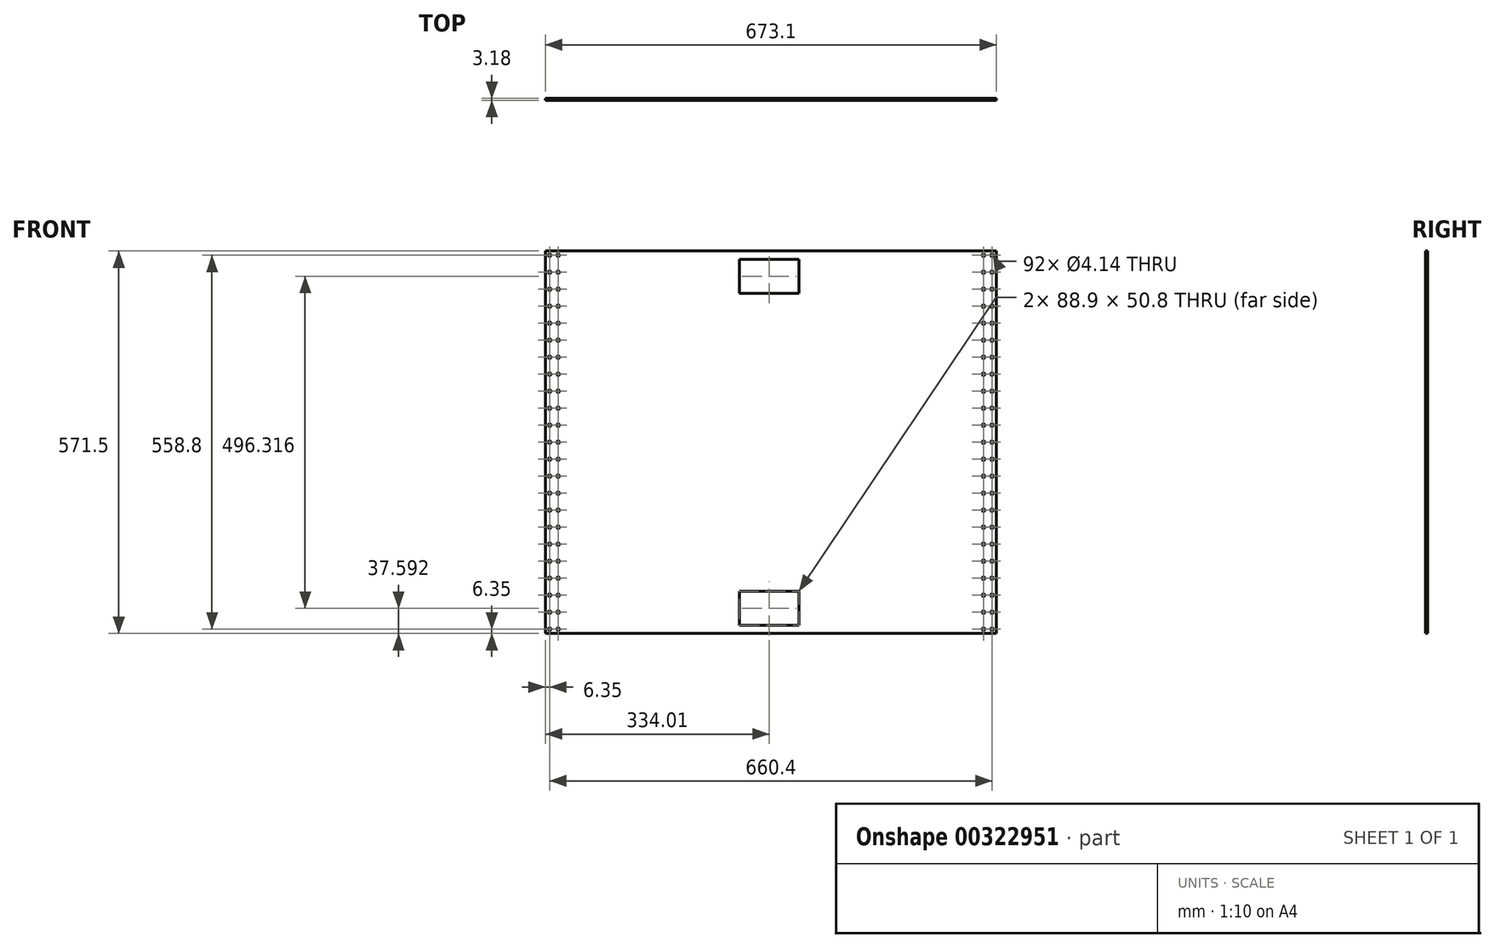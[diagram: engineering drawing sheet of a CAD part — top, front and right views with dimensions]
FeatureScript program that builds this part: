
annotation { "Feature Type Name" : "Feature", "Feature Type Description" : "" }
export const myFeature = defineFeature(function(context is Context, id is Id, definition is map)
    precondition{}
    {
        {
            var Q0;
            Q0=qCreatedBy(makeId("Front.planeOp"),FACE);
            var sketch = newSketch(context, id + "F0", { "sketchPlane" : qUnion([Q0])});
            skLineSegment(sketch, "E0.bottom", {"start": v(336.55, -285.75) * mm, "end": v(-336.55, -285.75) * mm});
            skLineSegment(sketch, "E0.top", {"start": v(336.55, 285.75) * mm, "end": v(-336.55, 285.75) * mm});
            skLineSegment(sketch, "E0.left", {"start": v(336.55, -285.75) * mm, "end": v(336.55, 285.75) * mm});
            skLineSegment(sketch, "E0.right", {"start": v(-336.55, -285.75) * mm, "end": v(-336.55, 285.75) * mm});
            skPoint(sketch, "E0.middle", {"position": v(0, 0) * mm});
            skSolve(sketch);
        }
        {
            var Q0;
            Q0 = qSketchRegion(id + "F0", true);
            extrude(context, id + "F1", {"entities" : qUnion([Q0]), "depth" : 3.17 * mm});
        }
        {
            var Q0;
            Q0=makeQuery(id+"F1.opExtrude","CAP_FACE",FACE,{"disambiguationData":[OSD([sQuery(id+"F0.wireOp",EDGE,"E0.bottom"),sQuery(id+"F0.wireOp",EDGE,"E0.top"),sQuery(id+"F0.wireOp",EDGE,"E0.left"),sQuery(id+"F0.wireOp",EDGE,"E0.right")])],"isStart":false});
            var sketch = newSketch(context, id + "F2", { "sketchPlane" : qUnion([Q0])});
            skCircle(sketch, "E1", {"center": v(330.2, -279.4) * mm, "radius": 2.07 * mm});
            skCircle(sketch, "E2.0.1.0", {"center": v(330.2, -254) * mm, "radius": 2.07 * mm});
            skCircle(sketch, "E2.0.2.0", {"center": v(330.2, -228.6) * mm, "radius": 2.07 * mm});
            skCircle(sketch, "E2.0.3.0", {"center": v(330.2, -203.2) * mm, "radius": 2.07 * mm});
            skCircle(sketch, "E2.0.4.0", {"center": v(330.2, -177.8) * mm, "radius": 2.07 * mm});
            skCircle(sketch, "E2.0.5.0", {"center": v(330.2, -152.4) * mm, "radius": 2.07 * mm});
            skCircle(sketch, "E2.1.0.0", {"center": v(317.5, -279.4) * mm, "radius": 2.07 * mm});
            skCircle(sketch, "E2.1.1.0", {"center": v(317.5, -254) * mm, "radius": 2.07 * mm});
            skCircle(sketch, "E2.1.2.0", {"center": v(317.5, -228.6) * mm, "radius": 2.07 * mm});
            skCircle(sketch, "E2.1.3.0", {"center": v(317.5, -203.2) * mm, "radius": 2.07 * mm});
            skCircle(sketch, "E2.1.4.0", {"center": v(317.5, -177.8) * mm, "radius": 2.07 * mm});
            skCircle(sketch, "E2.1.5.0", {"center": v(317.5, -152.4) * mm, "radius": 2.07 * mm});
            skLineSegment(sketch, "E2.direction1", {"start": v(330.2, -279.4) * mm, "end": v(317.5, -279.4) * mm, "construction": true});
            skLineSegment(sketch, "E2.direction2", {"start": v(330.2, -279.4) * mm, "end": v(330.2, -254) * mm, "construction": true});
            skCircle(sketch, "E3.0.0.6", {"center": v(330.2, -127) * mm, "radius": 2.07 * mm});
            skCircle(sketch, "E3.0.0.7", {"center": v(330.2, -101.6) * mm, "radius": 2.07 * mm});
            skCircle(sketch, "E3.0.0.8", {"center": v(330.2, -76.2) * mm, "radius": 2.07 * mm});
            skCircle(sketch, "E3.0.0.9", {"center": v(330.2, -50.8) * mm, "radius": 2.07 * mm});
            skCircle(sketch, "E3.0.0.10", {"center": v(330.2, -25.4) * mm, "radius": 2.07 * mm});
            skCircle(sketch, "E3.0.0.11", {"center": v(330.2, 0) * mm, "radius": 2.07 * mm});
            skCircle(sketch, "E3.0.0.12", {"center": v(330.2, 25.4) * mm, "radius": 2.07 * mm});
            skCircle(sketch, "E3.0.0.13", {"center": v(330.2, 50.8) * mm, "radius": 2.07 * mm});
            skCircle(sketch, "E3.0.0.14", {"center": v(330.2, 76.2) * mm, "radius": 2.07 * mm});
            skCircle(sketch, "E3.0.0.15", {"center": v(330.2, 101.6) * mm, "radius": 2.07 * mm});
            skCircle(sketch, "E3.0.0.16", {"center": v(330.2, 127) * mm, "radius": 2.07 * mm});
            skCircle(sketch, "E3.0.0.17", {"center": v(330.2, 152.4) * mm, "radius": 2.07 * mm});
            skCircle(sketch, "E3.0.0.18", {"center": v(330.2, 177.8) * mm, "radius": 2.07 * mm});
            skCircle(sketch, "E3.0.0.19", {"center": v(330.2, 203.2) * mm, "radius": 2.07 * mm});
            skCircle(sketch, "E3.0.1.6", {"center": v(317.5, -127) * mm, "radius": 2.07 * mm});
            skCircle(sketch, "E3.0.1.7", {"center": v(317.5, -101.6) * mm, "radius": 2.07 * mm});
            skCircle(sketch, "E3.0.1.8", {"center": v(317.5, -76.2) * mm, "radius": 2.07 * mm});
            skCircle(sketch, "E3.0.1.9", {"center": v(317.5, -50.8) * mm, "radius": 2.07 * mm});
            skCircle(sketch, "E3.0.1.10", {"center": v(317.5, -25.4) * mm, "radius": 2.07 * mm});
            skCircle(sketch, "E3.0.1.11", {"center": v(317.5, 0) * mm, "radius": 2.07 * mm});
            skCircle(sketch, "E3.0.1.12", {"center": v(317.5, 25.4) * mm, "radius": 2.07 * mm});
            skCircle(sketch, "E3.0.1.13", {"center": v(317.5, 50.8) * mm, "radius": 2.07 * mm});
            skCircle(sketch, "E3.0.1.14", {"center": v(317.5, 76.2) * mm, "radius": 2.07 * mm});
            skCircle(sketch, "E3.0.1.15", {"center": v(317.5, 101.6) * mm, "radius": 2.07 * mm});
            skCircle(sketch, "E3.0.1.16", {"center": v(317.5, 127) * mm, "radius": 2.07 * mm});
            skCircle(sketch, "E3.0.1.17", {"center": v(317.5, 152.4) * mm, "radius": 2.07 * mm});
            skCircle(sketch, "E3.0.1.18", {"center": v(317.5, 177.8) * mm, "radius": 2.07 * mm});
            skCircle(sketch, "E3.0.1.19", {"center": v(317.5, 203.2) * mm, "radius": 2.07 * mm});
            skCircle(sketch, "E4.0.0.20", {"center": v(330.2, 228.6) * mm, "radius": 2.07 * mm});
            skCircle(sketch, "E4.0.0.21", {"center": v(330.2, 254) * mm, "radius": 2.07 * mm});
            skCircle(sketch, "E4.0.0.22", {"center": v(330.2, 279.4) * mm, "radius": 2.07 * mm});
            skCircle(sketch, "E4.0.1.20", {"center": v(317.5, 228.6) * mm, "radius": 2.07 * mm});
            skCircle(sketch, "E4.0.1.21", {"center": v(317.5, 254) * mm, "radius": 2.07 * mm});
            skCircle(sketch, "E4.0.1.22", {"center": v(317.5, 279.4) * mm, "radius": 2.07 * mm});
            skCircle(sketch, "E5", {"center": v(-330.2, -279.4) * mm, "radius": 2.07 * mm});
            skCircle(sketch, "E6.0.1.0", {"center": v(-330.2, -254) * mm, "radius": 2.07 * mm});
            skCircle(sketch, "E6.0.2.0", {"center": v(-330.2, -228.6) * mm, "radius": 2.07 * mm});
            skCircle(sketch, "E6.0.3.0", {"center": v(-330.2, -203.2) * mm, "radius": 2.07 * mm});
            skCircle(sketch, "E6.0.4.0", {"center": v(-330.2, -177.8) * mm, "radius": 2.07 * mm});
            skCircle(sketch, "E6.0.5.0", {"center": v(-330.2, -152.4) * mm, "radius": 2.07 * mm});
            skCircle(sketch, "E6.0.6.0", {"center": v(-330.2, -127) * mm, "radius": 2.07 * mm});
            skCircle(sketch, "E6.0.7.0", {"center": v(-330.2, -101.6) * mm, "radius": 2.07 * mm});
            skCircle(sketch, "E6.0.8.0", {"center": v(-330.2, -76.2) * mm, "radius": 2.07 * mm});
            skCircle(sketch, "E6.0.9.0", {"center": v(-330.2, -50.8) * mm, "radius": 2.07 * mm});
            skCircle(sketch, "E6.0.10.0", {"center": v(-330.2, -25.4) * mm, "radius": 2.07 * mm});
            skCircle(sketch, "E6.0.11.0", {"center": v(-330.2, 0) * mm, "radius": 2.07 * mm});
            skCircle(sketch, "E6.0.12.0", {"center": v(-330.2, 25.4) * mm, "radius": 2.07 * mm});
            skCircle(sketch, "E6.0.13.0", {"center": v(-330.2, 50.8) * mm, "radius": 2.07 * mm});
            skCircle(sketch, "E6.0.14.0", {"center": v(-330.2, 76.2) * mm, "radius": 2.07 * mm});
            skCircle(sketch, "E6.0.15.0", {"center": v(-330.2, 101.6) * mm, "radius": 2.07 * mm});
            skCircle(sketch, "E6.0.16.0", {"center": v(-330.2, 127) * mm, "radius": 2.07 * mm});
            skCircle(sketch, "E6.0.17.0", {"center": v(-330.2, 152.4) * mm, "radius": 2.07 * mm});
            skCircle(sketch, "E6.0.18.0", {"center": v(-330.2, 177.8) * mm, "radius": 2.07 * mm});
            skCircle(sketch, "E6.0.19.0", {"center": v(-330.2, 203.2) * mm, "radius": 2.07 * mm});
            skCircle(sketch, "E6.0.20.0", {"center": v(-330.2, 228.6) * mm, "radius": 2.07 * mm});
            skCircle(sketch, "E6.0.21.0", {"center": v(-330.2, 254) * mm, "radius": 2.07 * mm});
            skCircle(sketch, "E6.0.22.0", {"center": v(-330.2, 279.4) * mm, "radius": 2.07 * mm});
            skCircle(sketch, "E6.1.0.0", {"center": v(-317.5, -279.4) * mm, "radius": 2.07 * mm});
            skCircle(sketch, "E6.1.1.0", {"center": v(-317.5, -254) * mm, "radius": 2.07 * mm});
            skCircle(sketch, "E6.1.2.0", {"center": v(-317.5, -228.6) * mm, "radius": 2.07 * mm});
            skCircle(sketch, "E6.1.3.0", {"center": v(-317.5, -203.2) * mm, "radius": 2.07 * mm});
            skCircle(sketch, "E6.1.4.0", {"center": v(-317.5, -177.8) * mm, "radius": 2.07 * mm});
            skCircle(sketch, "E6.1.5.0", {"center": v(-317.5, -152.4) * mm, "radius": 2.07 * mm});
            skCircle(sketch, "E6.1.6.0", {"center": v(-317.5, -127) * mm, "radius": 2.07 * mm});
            skCircle(sketch, "E6.1.7.0", {"center": v(-317.5, -101.6) * mm, "radius": 2.07 * mm});
            skCircle(sketch, "E6.1.8.0", {"center": v(-317.5, -76.2) * mm, "radius": 2.07 * mm});
            skCircle(sketch, "E6.1.9.0", {"center": v(-317.5, -50.8) * mm, "radius": 2.07 * mm});
            skCircle(sketch, "E6.1.10.0", {"center": v(-317.5, -25.4) * mm, "radius": 2.07 * mm});
            skCircle(sketch, "E6.1.11.0", {"center": v(-317.5, 0) * mm, "radius": 2.07 * mm});
            skCircle(sketch, "E6.1.12.0", {"center": v(-317.5, 25.4) * mm, "radius": 2.07 * mm});
            skCircle(sketch, "E6.1.13.0", {"center": v(-317.5, 50.8) * mm, "radius": 2.07 * mm});
            skCircle(sketch, "E6.1.14.0", {"center": v(-317.5, 76.2) * mm, "radius": 2.07 * mm});
            skCircle(sketch, "E6.1.15.0", {"center": v(-317.5, 101.6) * mm, "radius": 2.07 * mm});
            skCircle(sketch, "E6.1.16.0", {"center": v(-317.5, 127) * mm, "radius": 2.07 * mm});
            skCircle(sketch, "E6.1.17.0", {"center": v(-317.5, 152.4) * mm, "radius": 2.07 * mm});
            skCircle(sketch, "E6.1.18.0", {"center": v(-317.5, 177.8) * mm, "radius": 2.07 * mm});
            skCircle(sketch, "E6.1.19.0", {"center": v(-317.5, 203.2) * mm, "radius": 2.07 * mm});
            skCircle(sketch, "E6.1.20.0", {"center": v(-317.5, 228.6) * mm, "radius": 2.07 * mm});
            skCircle(sketch, "E6.1.21.0", {"center": v(-317.5, 254) * mm, "radius": 2.07 * mm});
            skCircle(sketch, "E6.1.22.0", {"center": v(-317.5, 279.4) * mm, "radius": 2.07 * mm});
            skLineSegment(sketch, "E6.direction1", {"start": v(-330.2, -279.4) * mm, "end": v(-317.5, -279.4) * mm, "construction": true});
            skLineSegment(sketch, "E6.direction2", {"start": v(-330.2, -279.4) * mm, "end": v(-330.2, -254) * mm, "construction": true});
            skSolve(sketch);
        }
        {
            var Q0;
            Q0=makeQuery(id+"F2.imprint","IMPRINT",FACE,{"disambiguationData":[TD([[makeQuery(id+"F2.imprint","IMPRINT",EDGE,{"derivedFrom":sQuery(id+"F2.wireOp",EDGE,"E5")}),1.0]])]});
            var Q1;
            Q1=makeQuery(id+"F2.imprint","IMPRINT",FACE,{"disambiguationData":[TD([[makeQuery(id+"F2.imprint","IMPRINT",EDGE,{"derivedFrom":sQuery(id+"F2.wireOp",EDGE,"E6.1.0.0")}),1.0]])]});
            var Q2;
            Q2=makeQuery(id+"F2.imprint","IMPRINT",FACE,{"disambiguationData":[TD([[makeQuery(id+"F2.imprint","IMPRINT",EDGE,{"derivedFrom":sQuery(id+"F2.wireOp",EDGE,"E6.1.1.0")}),1.0]])]});
            var Q3;
            Q3=makeQuery(id+"F2.imprint","IMPRINT",FACE,{"disambiguationData":[TD([[makeQuery(id+"F2.imprint","IMPRINT",EDGE,{"derivedFrom":sQuery(id+"F2.wireOp",EDGE,"E6.0.1.0")}),1.0]])]});
            var Q4;
            Q4=makeQuery(id+"F2.imprint","IMPRINT",FACE,{"disambiguationData":[TD([[makeQuery(id+"F2.imprint","IMPRINT",EDGE,{"derivedFrom":sQuery(id+"F2.wireOp",EDGE,"E6.0.2.0")}),1.0]])]});
            var Q5;
            Q5=makeQuery(id+"F2.imprint","IMPRINT",FACE,{"disambiguationData":[TD([[makeQuery(id+"F2.imprint","IMPRINT",EDGE,{"derivedFrom":sQuery(id+"F2.wireOp",EDGE,"E6.1.2.0")}),1.0]])]});
            var Q6;
            Q6=makeQuery(id+"F2.imprint","IMPRINT",FACE,{"disambiguationData":[TD([[makeQuery(id+"F2.imprint","IMPRINT",EDGE,{"derivedFrom":sQuery(id+"F2.wireOp",EDGE,"E6.1.3.0")}),1.0]])]});
            var Q7;
            Q7=makeQuery(id+"F2.imprint","IMPRINT",FACE,{"disambiguationData":[TD([[makeQuery(id+"F2.imprint","IMPRINT",EDGE,{"derivedFrom":sQuery(id+"F2.wireOp",EDGE,"E6.0.3.0")}),1.0]])]});
            var Q8;
            Q8=makeQuery(id+"F2.imprint","IMPRINT",FACE,{"disambiguationData":[TD([[makeQuery(id+"F2.imprint","IMPRINT",EDGE,{"derivedFrom":sQuery(id+"F2.wireOp",EDGE,"E6.0.4.0")}),1.0]])]});
            var Q9;
            Q9=makeQuery(id+"F2.imprint","IMPRINT",FACE,{"disambiguationData":[TD([[makeQuery(id+"F2.imprint","IMPRINT",EDGE,{"derivedFrom":sQuery(id+"F2.wireOp",EDGE,"E6.1.4.0")}),1.0]])]});
            var Q10;
            Q10=makeQuery(id+"F2.imprint","IMPRINT",FACE,{"disambiguationData":[TD([[makeQuery(id+"F2.imprint","IMPRINT",EDGE,{"derivedFrom":sQuery(id+"F2.wireOp",EDGE,"E6.1.5.0")}),1.0]])]});
            var Q11;
            Q11=makeQuery(id+"F2.imprint","IMPRINT",FACE,{"disambiguationData":[TD([[makeQuery(id+"F2.imprint","IMPRINT",EDGE,{"derivedFrom":sQuery(id+"F2.wireOp",EDGE,"E6.0.5.0")}),1.0]])]});
            var Q12;
            Q12=makeQuery(id+"F2.imprint","IMPRINT",FACE,{"disambiguationData":[TD([[makeQuery(id+"F2.imprint","IMPRINT",EDGE,{"derivedFrom":sQuery(id+"F2.wireOp",EDGE,"E6.0.6.0")}),1.0]])]});
            var Q13;
            Q13=makeQuery(id+"F2.imprint","IMPRINT",FACE,{"disambiguationData":[TD([[makeQuery(id+"F2.imprint","IMPRINT",EDGE,{"derivedFrom":sQuery(id+"F2.wireOp",EDGE,"E6.1.6.0")}),1.0]])]});
            var Q14;
            Q14=makeQuery(id+"F2.imprint","IMPRINT",FACE,{"disambiguationData":[TD([[makeQuery(id+"F2.imprint","IMPRINT",EDGE,{"derivedFrom":sQuery(id+"F2.wireOp",EDGE,"E6.1.7.0")}),1.0]])]});
            var Q15;
            Q15=makeQuery(id+"F2.imprint","IMPRINT",FACE,{"disambiguationData":[TD([[makeQuery(id+"F2.imprint","IMPRINT",EDGE,{"derivedFrom":sQuery(id+"F2.wireOp",EDGE,"E6.0.7.0")}),1.0]])]});
            var Q16;
            Q16=makeQuery(id+"F2.imprint","IMPRINT",FACE,{"disambiguationData":[TD([[makeQuery(id+"F2.imprint","IMPRINT",EDGE,{"derivedFrom":sQuery(id+"F2.wireOp",EDGE,"E6.0.8.0")}),1.0]])]});
            var Q17;
            Q17=makeQuery(id+"F2.imprint","IMPRINT",FACE,{"disambiguationData":[TD([[makeQuery(id+"F2.imprint","IMPRINT",EDGE,{"derivedFrom":sQuery(id+"F2.wireOp",EDGE,"E6.1.8.0")}),1.0]])]});
            var Q18;
            Q18=makeQuery(id+"F2.imprint","IMPRINT",FACE,{"disambiguationData":[TD([[makeQuery(id+"F2.imprint","IMPRINT",EDGE,{"derivedFrom":sQuery(id+"F2.wireOp",EDGE,"E6.1.9.0")}),1.0]])]});
            var Q19;
            Q19=makeQuery(id+"F2.imprint","IMPRINT",FACE,{"disambiguationData":[TD([[makeQuery(id+"F2.imprint","IMPRINT",EDGE,{"derivedFrom":sQuery(id+"F2.wireOp",EDGE,"E6.0.9.0")}),1.0]])]});
            var Q20;
            Q20=makeQuery(id+"F2.imprint","IMPRINT",FACE,{"disambiguationData":[TD([[makeQuery(id+"F2.imprint","IMPRINT",EDGE,{"derivedFrom":sQuery(id+"F2.wireOp",EDGE,"E6.0.10.0")}),1.0]])]});
            var Q21;
            Q21=makeQuery(id+"F2.imprint","IMPRINT",FACE,{"disambiguationData":[TD([[makeQuery(id+"F2.imprint","IMPRINT",EDGE,{"derivedFrom":sQuery(id+"F2.wireOp",EDGE,"E6.1.10.0")}),1.0]])]});
            var Q22;
            Q22=makeQuery(id+"F2.imprint","IMPRINT",FACE,{"disambiguationData":[TD([[makeQuery(id+"F2.imprint","IMPRINT",EDGE,{"derivedFrom":sQuery(id+"F2.wireOp",EDGE,"E6.0.11.0")}),1.0]])]});
            var Q23;
            Q23=makeQuery(id+"F2.imprint","IMPRINT",FACE,{"disambiguationData":[TD([[makeQuery(id+"F2.imprint","IMPRINT",EDGE,{"derivedFrom":sQuery(id+"F2.wireOp",EDGE,"E6.1.11.0")}),1.0]])]});
            var Q24;
            Q24=makeQuery(id+"F2.imprint","IMPRINT",FACE,{"disambiguationData":[TD([[makeQuery(id+"F2.imprint","IMPRINT",EDGE,{"derivedFrom":sQuery(id+"F2.wireOp",EDGE,"E6.1.12.0")}),1.0]])]});
            var Q25;
            Q25=makeQuery(id+"F2.imprint","IMPRINT",FACE,{"disambiguationData":[TD([[makeQuery(id+"F2.imprint","IMPRINT",EDGE,{"derivedFrom":sQuery(id+"F2.wireOp",EDGE,"E6.0.12.0")}),1.0]])]});
            var Q26;
            Q26=makeQuery(id+"F2.imprint","IMPRINT",FACE,{"disambiguationData":[TD([[makeQuery(id+"F2.imprint","IMPRINT",EDGE,{"derivedFrom":sQuery(id+"F2.wireOp",EDGE,"E6.0.13.0")}),1.0]])]});
            var Q27;
            Q27=makeQuery(id+"F2.imprint","IMPRINT",FACE,{"disambiguationData":[TD([[makeQuery(id+"F2.imprint","IMPRINT",EDGE,{"derivedFrom":sQuery(id+"F2.wireOp",EDGE,"E6.1.13.0")}),1.0]])]});
            var Q28;
            Q28=makeQuery(id+"F2.imprint","IMPRINT",FACE,{"disambiguationData":[TD([[makeQuery(id+"F2.imprint","IMPRINT",EDGE,{"derivedFrom":sQuery(id+"F2.wireOp",EDGE,"E6.1.14.0")}),1.0]])]});
            var Q29;
            Q29=makeQuery(id+"F2.imprint","IMPRINT",FACE,{"disambiguationData":[TD([[makeQuery(id+"F2.imprint","IMPRINT",EDGE,{"derivedFrom":sQuery(id+"F2.wireOp",EDGE,"E6.0.14.0")}),1.0]])]});
            var Q30;
            Q30=makeQuery(id+"F2.imprint","IMPRINT",FACE,{"disambiguationData":[TD([[makeQuery(id+"F2.imprint","IMPRINT",EDGE,{"derivedFrom":sQuery(id+"F2.wireOp",EDGE,"E6.0.15.0")}),1.0]])]});
            var Q31;
            Q31=makeQuery(id+"F2.imprint","IMPRINT",FACE,{"disambiguationData":[TD([[makeQuery(id+"F2.imprint","IMPRINT",EDGE,{"derivedFrom":sQuery(id+"F2.wireOp",EDGE,"E6.1.15.0")}),1.0]])]});
            var Q32;
            Q32=makeQuery(id+"F2.imprint","IMPRINT",FACE,{"disambiguationData":[TD([[makeQuery(id+"F2.imprint","IMPRINT",EDGE,{"derivedFrom":sQuery(id+"F2.wireOp",EDGE,"E6.0.16.0")}),1.0]])]});
            var Q33;
            Q33=makeQuery(id+"F2.imprint","IMPRINT",FACE,{"disambiguationData":[TD([[makeQuery(id+"F2.imprint","IMPRINT",EDGE,{"derivedFrom":sQuery(id+"F2.wireOp",EDGE,"E6.1.16.0")}),1.0]])]});
            var Q34;
            Q34=makeQuery(id+"F2.imprint","IMPRINT",FACE,{"disambiguationData":[TD([[makeQuery(id+"F2.imprint","IMPRINT",EDGE,{"derivedFrom":sQuery(id+"F2.wireOp",EDGE,"E6.1.17.0")}),1.0]])]});
            var Q35;
            Q35=makeQuery(id+"F2.imprint","IMPRINT",FACE,{"disambiguationData":[TD([[makeQuery(id+"F2.imprint","IMPRINT",EDGE,{"derivedFrom":sQuery(id+"F2.wireOp",EDGE,"E6.0.17.0")}),1.0]])]});
            var Q36;
            Q36=makeQuery(id+"F2.imprint","IMPRINT",FACE,{"disambiguationData":[TD([[makeQuery(id+"F2.imprint","IMPRINT",EDGE,{"derivedFrom":sQuery(id+"F2.wireOp",EDGE,"E6.0.18.0")}),1.0]])]});
            var Q37;
            Q37=makeQuery(id+"F2.imprint","IMPRINT",FACE,{"disambiguationData":[TD([[makeQuery(id+"F2.imprint","IMPRINT",EDGE,{"derivedFrom":sQuery(id+"F2.wireOp",EDGE,"E6.1.18.0")}),1.0]])]});
            var Q38;
            Q38=makeQuery(id+"F2.imprint","IMPRINT",FACE,{"disambiguationData":[TD([[makeQuery(id+"F2.imprint","IMPRINT",EDGE,{"derivedFrom":sQuery(id+"F2.wireOp",EDGE,"E6.1.19.0")}),1.0]])]});
            var Q39;
            Q39=makeQuery(id+"F2.imprint","IMPRINT",FACE,{"disambiguationData":[TD([[makeQuery(id+"F2.imprint","IMPRINT",EDGE,{"derivedFrom":sQuery(id+"F2.wireOp",EDGE,"E6.0.19.0")}),1.0]])]});
            var Q40;
            Q40=makeQuery(id+"F2.imprint","IMPRINT",FACE,{"disambiguationData":[TD([[makeQuery(id+"F2.imprint","IMPRINT",EDGE,{"derivedFrom":sQuery(id+"F2.wireOp",EDGE,"E6.0.20.0")}),1.0]])]});
            var Q41;
            Q41=makeQuery(id+"F2.imprint","IMPRINT",FACE,{"disambiguationData":[TD([[makeQuery(id+"F2.imprint","IMPRINT",EDGE,{"derivedFrom":sQuery(id+"F2.wireOp",EDGE,"E6.1.20.0")}),1.0]])]});
            var Q42;
            Q42=makeQuery(id+"F2.imprint","IMPRINT",FACE,{"disambiguationData":[TD([[makeQuery(id+"F2.imprint","IMPRINT",EDGE,{"derivedFrom":sQuery(id+"F2.wireOp",EDGE,"E6.1.21.0")}),1.0]])]});
            var Q43;
            Q43=makeQuery(id+"F2.imprint","IMPRINT",FACE,{"disambiguationData":[TD([[makeQuery(id+"F2.imprint","IMPRINT",EDGE,{"derivedFrom":sQuery(id+"F2.wireOp",EDGE,"E6.0.21.0")}),1.0]])]});
            var Q44;
            Q44=makeQuery(id+"F2.imprint","IMPRINT",FACE,{"disambiguationData":[TD([[makeQuery(id+"F2.imprint","IMPRINT",EDGE,{"derivedFrom":sQuery(id+"F2.wireOp",EDGE,"E6.0.22.0")}),1.0]])]});
            var Q45;
            Q45=makeQuery(id+"F2.imprint","IMPRINT",FACE,{"disambiguationData":[TD([[makeQuery(id+"F2.imprint","IMPRINT",EDGE,{"derivedFrom":sQuery(id+"F2.wireOp",EDGE,"E6.1.22.0")}),1.0]])]});
            var Q46;
            Q46=makeQuery(id+"F2.imprint","IMPRINT",FACE,{"disambiguationData":[TD([[makeQuery(id+"F2.imprint","IMPRINT",EDGE,{"derivedFrom":sQuery(id+"F2.wireOp",EDGE,"E4.0.1.22")}),1.0]])]});
            var Q47;
            Q47=makeQuery(id+"F2.imprint","IMPRINT",FACE,{"disambiguationData":[TD([[makeQuery(id+"F2.imprint","IMPRINT",EDGE,{"derivedFrom":sQuery(id+"F2.wireOp",EDGE,"E4.0.0.22")}),1.0]])]});
            var Q48;
            Q48=makeQuery(id+"F2.imprint","IMPRINT",FACE,{"disambiguationData":[TD([[makeQuery(id+"F2.imprint","IMPRINT",EDGE,{"derivedFrom":sQuery(id+"F2.wireOp",EDGE,"E4.0.1.21")}),1.0]])]});
            var Q49;
            Q49=makeQuery(id+"F2.imprint","IMPRINT",FACE,{"disambiguationData":[TD([[makeQuery(id+"F2.imprint","IMPRINT",EDGE,{"derivedFrom":sQuery(id+"F2.wireOp",EDGE,"E4.0.0.21")}),1.0]])]});
            var Q50;
            Q50=makeQuery(id+"F2.imprint","IMPRINT",FACE,{"disambiguationData":[TD([[makeQuery(id+"F2.imprint","IMPRINT",EDGE,{"derivedFrom":sQuery(id+"F2.wireOp",EDGE,"E4.0.1.20")}),1.0]])]});
            var Q51;
            Q51=makeQuery(id+"F2.imprint","IMPRINT",FACE,{"disambiguationData":[TD([[makeQuery(id+"F2.imprint","IMPRINT",EDGE,{"derivedFrom":sQuery(id+"F2.wireOp",EDGE,"E4.0.0.20")}),1.0]])]});
            var Q52;
            Q52=makeQuery(id+"F2.imprint","IMPRINT",FACE,{"disambiguationData":[TD([[makeQuery(id+"F2.imprint","IMPRINT",EDGE,{"derivedFrom":sQuery(id+"F2.wireOp",EDGE,"E3.0.1.19")}),1.0]])]});
            var Q53;
            Q53=makeQuery(id+"F2.imprint","IMPRINT",FACE,{"disambiguationData":[TD([[makeQuery(id+"F2.imprint","IMPRINT",EDGE,{"derivedFrom":sQuery(id+"F2.wireOp",EDGE,"E3.0.0.19")}),1.0]])]});
            var Q54;
            Q54=makeQuery(id+"F2.imprint","IMPRINT",FACE,{"disambiguationData":[TD([[makeQuery(id+"F2.imprint","IMPRINT",EDGE,{"derivedFrom":sQuery(id+"F2.wireOp",EDGE,"E3.0.1.18")}),1.0]])]});
            var Q55;
            Q55=makeQuery(id+"F2.imprint","IMPRINT",FACE,{"disambiguationData":[TD([[makeQuery(id+"F2.imprint","IMPRINT",EDGE,{"derivedFrom":sQuery(id+"F2.wireOp",EDGE,"E3.0.0.18")}),1.0]])]});
            var Q56;
            Q56=makeQuery(id+"F2.imprint","IMPRINT",FACE,{"disambiguationData":[TD([[makeQuery(id+"F2.imprint","IMPRINT",EDGE,{"derivedFrom":sQuery(id+"F2.wireOp",EDGE,"E3.0.0.17")}),1.0]])]});
            var Q57;
            Q57=makeQuery(id+"F2.imprint","IMPRINT",FACE,{"disambiguationData":[TD([[makeQuery(id+"F2.imprint","IMPRINT",EDGE,{"derivedFrom":sQuery(id+"F2.wireOp",EDGE,"E3.0.1.17")}),1.0]])]});
            var Q58;
            Q58=makeQuery(id+"F2.imprint","IMPRINT",FACE,{"disambiguationData":[TD([[makeQuery(id+"F2.imprint","IMPRINT",EDGE,{"derivedFrom":sQuery(id+"F2.wireOp",EDGE,"E3.0.1.16")}),1.0]])]});
            var Q59;
            Q59=makeQuery(id+"F2.imprint","IMPRINT",FACE,{"disambiguationData":[TD([[makeQuery(id+"F2.imprint","IMPRINT",EDGE,{"derivedFrom":sQuery(id+"F2.wireOp",EDGE,"E3.0.0.16")}),1.0]])]});
            var Q60;
            Q60=makeQuery(id+"F2.imprint","IMPRINT",FACE,{"disambiguationData":[TD([[makeQuery(id+"F2.imprint","IMPRINT",EDGE,{"derivedFrom":sQuery(id+"F2.wireOp",EDGE,"E3.0.1.15")}),1.0]])]});
            var Q61;
            Q61=makeQuery(id+"F2.imprint","IMPRINT",FACE,{"disambiguationData":[TD([[makeQuery(id+"F2.imprint","IMPRINT",EDGE,{"derivedFrom":sQuery(id+"F2.wireOp",EDGE,"E3.0.0.15")}),1.0]])]});
            var Q62;
            Q62=makeQuery(id+"F2.imprint","IMPRINT",FACE,{"disambiguationData":[TD([[makeQuery(id+"F2.imprint","IMPRINT",EDGE,{"derivedFrom":sQuery(id+"F2.wireOp",EDGE,"E3.0.0.14")}),1.0]])]});
            var Q63;
            Q63=makeQuery(id+"F2.imprint","IMPRINT",FACE,{"disambiguationData":[TD([[makeQuery(id+"F2.imprint","IMPRINT",EDGE,{"derivedFrom":sQuery(id+"F2.wireOp",EDGE,"E3.0.1.14")}),1.0]])]});
            var Q64;
            Q64=makeQuery(id+"F2.imprint","IMPRINT",FACE,{"disambiguationData":[TD([[makeQuery(id+"F2.imprint","IMPRINT",EDGE,{"derivedFrom":sQuery(id+"F2.wireOp",EDGE,"E3.0.1.13")}),1.0]])]});
            var Q65;
            Q65=makeQuery(id+"F2.imprint","IMPRINT",FACE,{"disambiguationData":[TD([[makeQuery(id+"F2.imprint","IMPRINT",EDGE,{"derivedFrom":sQuery(id+"F2.wireOp",EDGE,"E3.0.0.13")}),1.0]])]});
            var Q66;
            Q66=makeQuery(id+"F2.imprint","IMPRINT",FACE,{"disambiguationData":[TD([[makeQuery(id+"F2.imprint","IMPRINT",EDGE,{"derivedFrom":sQuery(id+"F2.wireOp",EDGE,"E3.0.0.12")}),1.0]])]});
            var Q67;
            Q67=makeQuery(id+"F2.imprint","IMPRINT",FACE,{"disambiguationData":[TD([[makeQuery(id+"F2.imprint","IMPRINT",EDGE,{"derivedFrom":sQuery(id+"F2.wireOp",EDGE,"E3.0.1.12")}),1.0]])]});
            var Q68;
            Q68=makeQuery(id+"F2.imprint","IMPRINT",FACE,{"disambiguationData":[TD([[makeQuery(id+"F2.imprint","IMPRINT",EDGE,{"derivedFrom":sQuery(id+"F2.wireOp",EDGE,"E3.0.1.11")}),1.0]])]});
            var Q69;
            Q69=makeQuery(id+"F2.imprint","IMPRINT",FACE,{"disambiguationData":[TD([[makeQuery(id+"F2.imprint","IMPRINT",EDGE,{"derivedFrom":sQuery(id+"F2.wireOp",EDGE,"E3.0.0.11")}),1.0]])]});
            var Q70;
            Q70=makeQuery(id+"F2.imprint","IMPRINT",FACE,{"disambiguationData":[TD([[makeQuery(id+"F2.imprint","IMPRINT",EDGE,{"derivedFrom":sQuery(id+"F2.wireOp",EDGE,"E3.0.0.10")}),1.0]])]});
            var Q71;
            Q71=makeQuery(id+"F2.imprint","IMPRINT",FACE,{"disambiguationData":[TD([[makeQuery(id+"F2.imprint","IMPRINT",EDGE,{"derivedFrom":sQuery(id+"F2.wireOp",EDGE,"E3.0.1.10")}),1.0]])]});
            var Q72;
            Q72=makeQuery(id+"F2.imprint","IMPRINT",FACE,{"disambiguationData":[TD([[makeQuery(id+"F2.imprint","IMPRINT",EDGE,{"derivedFrom":sQuery(id+"F2.wireOp",EDGE,"E3.0.1.9")}),1.0]])]});
            var Q73;
            Q73=makeQuery(id+"F2.imprint","IMPRINT",FACE,{"disambiguationData":[TD([[makeQuery(id+"F2.imprint","IMPRINT",EDGE,{"derivedFrom":sQuery(id+"F2.wireOp",EDGE,"E3.0.0.9")}),1.0]])]});
            var Q74;
            Q74=makeQuery(id+"F2.imprint","IMPRINT",FACE,{"disambiguationData":[TD([[makeQuery(id+"F2.imprint","IMPRINT",EDGE,{"derivedFrom":sQuery(id+"F2.wireOp",EDGE,"E3.0.0.8")}),1.0]])]});
            var Q75;
            Q75=makeQuery(id+"F2.imprint","IMPRINT",FACE,{"disambiguationData":[TD([[makeQuery(id+"F2.imprint","IMPRINT",EDGE,{"derivedFrom":sQuery(id+"F2.wireOp",EDGE,"E3.0.1.8")}),1.0]])]});
            var Q76;
            Q76=makeQuery(id+"F2.imprint","IMPRINT",FACE,{"disambiguationData":[TD([[makeQuery(id+"F2.imprint","IMPRINT",EDGE,{"derivedFrom":sQuery(id+"F2.wireOp",EDGE,"E3.0.1.7")}),1.0]])]});
            var Q77;
            Q77=makeQuery(id+"F2.imprint","IMPRINT",FACE,{"disambiguationData":[TD([[makeQuery(id+"F2.imprint","IMPRINT",EDGE,{"derivedFrom":sQuery(id+"F2.wireOp",EDGE,"E3.0.0.7")}),1.0]])]});
            var Q78;
            Q78=makeQuery(id+"F2.imprint","IMPRINT",FACE,{"disambiguationData":[TD([[makeQuery(id+"F2.imprint","IMPRINT",EDGE,{"derivedFrom":sQuery(id+"F2.wireOp",EDGE,"E3.0.1.6")}),1.0]])]});
            var Q79;
            Q79=makeQuery(id+"F2.imprint","IMPRINT",FACE,{"disambiguationData":[TD([[makeQuery(id+"F2.imprint","IMPRINT",EDGE,{"derivedFrom":sQuery(id+"F2.wireOp",EDGE,"E3.0.0.6")}),1.0]])]});
            var Q80;
            Q80=makeQuery(id+"F2.imprint","IMPRINT",FACE,{"disambiguationData":[TD([[makeQuery(id+"F2.imprint","IMPRINT",EDGE,{"derivedFrom":sQuery(id+"F2.wireOp",EDGE,"E2.0.5.0")}),1.0]])]});
            var Q81;
            Q81=makeQuery(id+"F2.imprint","IMPRINT",FACE,{"disambiguationData":[TD([[makeQuery(id+"F2.imprint","IMPRINT",EDGE,{"derivedFrom":sQuery(id+"F2.wireOp",EDGE,"E2.1.5.0")}),1.0]])]});
            var Q82;
            Q82=makeQuery(id+"F2.imprint","IMPRINT",FACE,{"disambiguationData":[TD([[makeQuery(id+"F2.imprint","IMPRINT",EDGE,{"derivedFrom":sQuery(id+"F2.wireOp",EDGE,"E2.1.4.0")}),1.0]])]});
            var Q83;
            Q83=makeQuery(id+"F2.imprint","IMPRINT",FACE,{"disambiguationData":[TD([[makeQuery(id+"F2.imprint","IMPRINT",EDGE,{"derivedFrom":sQuery(id+"F2.wireOp",EDGE,"E2.0.4.0")}),1.0]])]});
            var Q84;
            Q84=makeQuery(id+"F2.imprint","IMPRINT",FACE,{"disambiguationData":[TD([[makeQuery(id+"F2.imprint","IMPRINT",EDGE,{"derivedFrom":sQuery(id+"F2.wireOp",EDGE,"E2.0.3.0")}),1.0]])]});
            var Q85;
            Q85=makeQuery(id+"F2.imprint","IMPRINT",FACE,{"disambiguationData":[TD([[makeQuery(id+"F2.imprint","IMPRINT",EDGE,{"derivedFrom":sQuery(id+"F2.wireOp",EDGE,"E2.1.3.0")}),1.0]])]});
            var Q86;
            Q86=makeQuery(id+"F2.imprint","IMPRINT",FACE,{"disambiguationData":[TD([[makeQuery(id+"F2.imprint","IMPRINT",EDGE,{"derivedFrom":sQuery(id+"F2.wireOp",EDGE,"E2.1.2.0")}),1.0]])]});
            var Q87;
            Q87=makeQuery(id+"F2.imprint","IMPRINT",FACE,{"disambiguationData":[TD([[makeQuery(id+"F2.imprint","IMPRINT",EDGE,{"derivedFrom":sQuery(id+"F2.wireOp",EDGE,"E2.1.1.0")}),1.0]])]});
            var Q88;
            Q88=makeQuery(id+"F2.imprint","IMPRINT",FACE,{"disambiguationData":[TD([[makeQuery(id+"F2.imprint","IMPRINT",EDGE,{"derivedFrom":sQuery(id+"F2.wireOp",EDGE,"E2.1.0.0")}),1.0]])]});
            var Q89;
            Q89=makeQuery(id+"F2.imprint","IMPRINT",FACE,{"disambiguationData":[TD([[makeQuery(id+"F2.imprint","IMPRINT",EDGE,{"derivedFrom":sQuery(id+"F2.wireOp",EDGE,"E1")}),1.0]])]});
            var Q90;
            Q90=makeQuery(id+"F2.imprint","IMPRINT",FACE,{"disambiguationData":[TD([[makeQuery(id+"F2.imprint","IMPRINT",EDGE,{"derivedFrom":sQuery(id+"F2.wireOp",EDGE,"E2.0.1.0")}),1.0]])]});
            var Q91;
            Q91=makeQuery(id+"F2.imprint","IMPRINT",FACE,{"disambiguationData":[TD([[makeQuery(id+"F2.imprint","IMPRINT",EDGE,{"derivedFrom":sQuery(id+"F2.wireOp",EDGE,"E2.0.2.0")}),1.0]])]});
            var Q92;
            Q92=sQuery(id+"F2.wireOp",EDGE,"E5");
            extrude(context, id + "F3", {"entities" : qUnion([Q0, Q1, Q2, Q3, Q4, Q5, Q6, Q7, Q8, Q9, Q10, Q11, Q12, Q13, Q14, Q15, Q16, Q17, Q18, Q19, Q20, Q21, Q22, Q23, Q24, Q25, Q26, Q27, Q28, Q29, Q30, Q31, Q32, Q33, Q34, Q35, Q36, Q37, Q38, Q39, Q40, Q41, Q42, Q43, Q44, Q45, Q46, Q47, Q48, Q49, Q50, Q51, Q52, Q53, Q54, Q55, Q56, Q57, Q58, Q59, Q60, Q61, Q62, Q63, Q64, Q65, Q66, Q67, Q68, Q69, Q70, Q71, Q72, Q73, Q74, Q75, Q76, Q77, Q78, Q79, Q80, Q81, Q82, Q83, Q84, Q85, Q86, Q87, Q88, Q89, Q90, Q91]), "operationType" : NewBodyOperationType.REMOVE, "surfaceEntities" : qUnion([Q92]), "oppositeDirection" : true, "depth" : 25.4 * mm});
        }
        {
            var Q0;
            Q0=makeQuery(id+"F1.opExtrude","CAP_FACE",FACE,{"disambiguationData":[OSD([sQuery(id+"F0.wireOp",EDGE,"E0.bottom"),sQuery(id+"F0.wireOp",EDGE,"E0.top"),sQuery(id+"F0.wireOp",EDGE,"E0.left"),sQuery(id+"F0.wireOp",EDGE,"E0.right")])],"isStart":false});
            var sketch = newSketch(context, id + "F4", { "sketchPlane" : qUnion([Q0])});
            skLineSegment(sketch, "E7.bottom", {"start": v(41.91, -273.56) * mm, "end": v(-46.99, -273.56) * mm});
            skLineSegment(sketch, "E7.top", {"start": v(41.91, -222.76) * mm, "end": v(-46.99, -222.76) * mm});
            skLineSegment(sketch, "E7.left", {"start": v(41.91, -273.56) * mm, "end": v(41.91, -222.76) * mm});
            skLineSegment(sketch, "E7.right", {"start": v(-46.99, -273.56) * mm, "end": v(-46.99, -222.76) * mm});
            skPoint(sketch, "E7.middle", {"position": v(-2.54, -248.16) * mm});
            skPoint(sketch, "E8.middle", {"position": v(-2.54, 248.16) * mm});
            skLineSegment(sketch, "E9.bottom", {"start": v(41.9, 222.76) * mm, "end": v(-47, 222.76) * mm});
            skLineSegment(sketch, "E9.top", {"start": v(41.9, 273.56) * mm, "end": v(-47, 273.56) * mm});
            skLineSegment(sketch, "E9.left", {"start": v(41.9, 222.76) * mm, "end": v(41.9, 273.56) * mm});
            skLineSegment(sketch, "E9.right", {"start": v(-47, 222.76) * mm, "end": v(-47, 273.56) * mm});
            skSolve(sketch);
        }
        {
            var Q0;
            Q0 = qSketchRegion(id + "F4", true);
            extrude(context, id + "F5", {"entities" : qUnion([Q0]), "operationType" : NewBodyOperationType.REMOVE, "oppositeDirection" : true, "depth" : 25.4 * mm});
        }
    });
